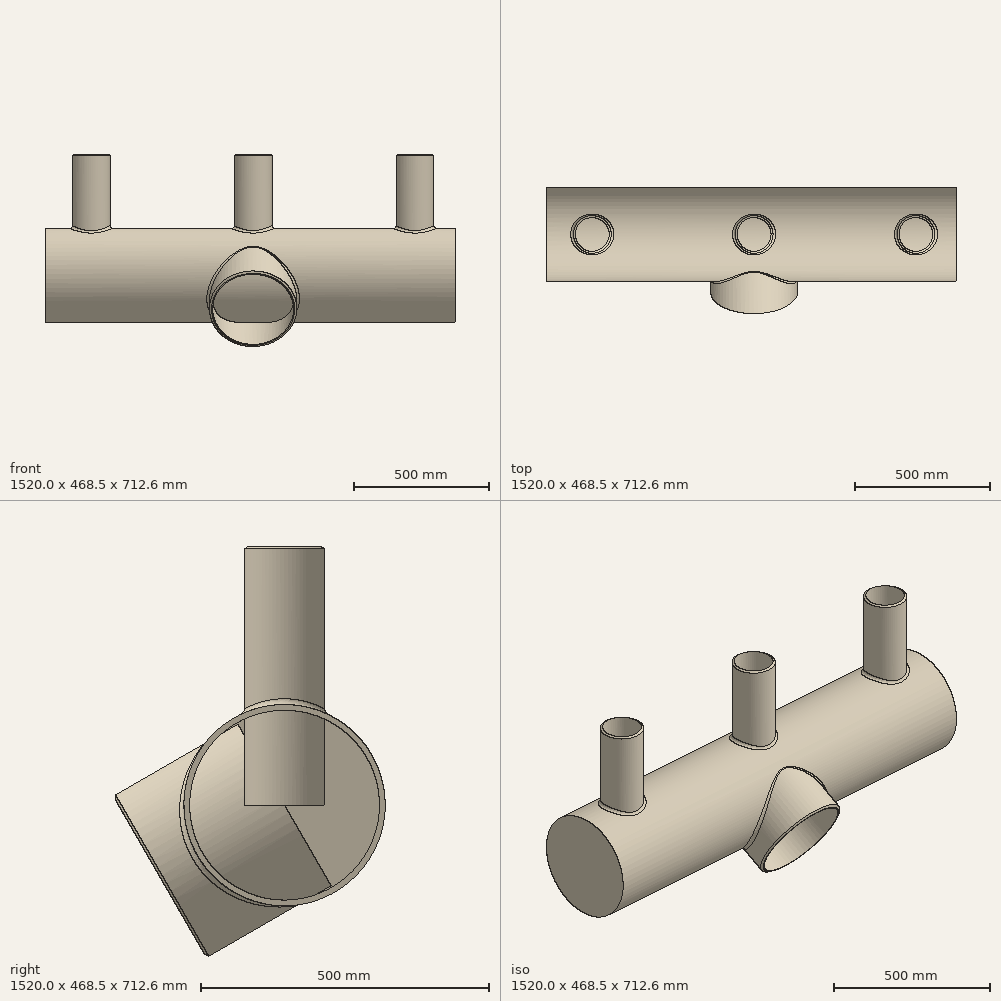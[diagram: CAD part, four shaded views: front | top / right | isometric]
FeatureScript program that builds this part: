
annotation { "Feature Type Name" : "Feature", "Feature Type Description" : "" }
export const myFeature = defineFeature(function(context is Context, id is Id, definition is map)
    precondition{}
    {
        {
            var Q0;
            Q0=qCreatedBy(makeId("Right.planeOp"),FACE);
            var sketch = newSketch(context, id + "F0", { "sketchPlane" : qUnion([Q0])});
            skCircle(sketch, "E0", {"center": v(0, 0) * mm, "radius": 175 * mm});
            skCircle(sketch, "E1", {"center": v(0, 0) * mm, "radius": 165 * mm});
            skSolve(sketch);
        }
        {
            var Q0;
            Q0=makeQuery(id+"F0.imprint","IMPRINT",FACE,{"disambiguationData":[TD([[makeQuery(id+"F0.imprint","IMPRINT",EDGE,{"derivedFrom":sQuery(id+"F0.wireOp",EDGE,"E0")}),1.0]])]});
            extrude(context, id + "F1", {"entities" : qUnion([Q0]), "endBound" : BoundingType.SYMMETRIC, "depth" : 1500 * mm, "offsetDistance" : 25 * mm});
        }
        {
            var Q0;
            Q0=makeQuery(id+"F1.opExtrude","CAP_FACE",FACE,{"disambiguationData":[OSD([sQuery(id+"F0.wireOp",EDGE,"E0"),sQuery(id+"F0.wireOp",EDGE,"E1")])],"isStart":true});
            var sketch = newSketch(context, id + "F2", { "sketchPlane" : qUnion([Q0])});
            skCircle(sketch, "E2.0", {"center": v(0, 0) * mm, "radius": 175 * mm});
            skSolve(sketch);
        }
        {
            var Q0;
            Q0 = qSketchRegion(id + "F2", true);
            extrude(context, id + "F3", {"entities" : qUnion([Q0]), "operationType" : NewBodyOperationType.ADD, "depth" : 20 * mm, "offsetDistance" : 25 * mm});
        }
        {
            var Q0;
            Q0=qCreatedBy(makeId("Top.planeOp"),FACE);
            var sketch = newSketch(context, id + "F4", { "sketchPlane" : qUnion([Q0])});
            skCircle(sketch, "E3", {"center": v(-600, 0) * mm, "radius": 69.85 * mm});
            skCircle(sketch, "E4", {"center": v(0, 0) * mm, "radius": 69.85 * mm});
            skCircle(sketch, "E5", {"center": v(600, 0) * mm, "radius": 69.85 * mm});
            skCircle(sketch, "E6", {"center": v(-600, 0) * mm, "radius": 62.5 * mm});
            skCircle(sketch, "E7", {"center": v(0, 0) * mm, "radius": 62.5 * mm});
            skCircle(sketch, "E8", {"center": v(600, 0) * mm, "radius": 62.5 * mm});
            skSolve(sketch);
        }
        {
            var Q0;
            Q0 = qSketchRegion(id + "F4", true);
            extrude(context, id + "F5", {"entities" : qUnion([Q0]), "operationType" : NewBodyOperationType.ADD, "depth" : 450 * mm, "offsetDistance" : 25 * mm});
        }
        {
            var Q0;
            Q0=qCreatedBy(makeId("Top.planeOp"),FACE);
            var sketch = newSketch(context, id + "F6", { "sketchPlane" : qUnion([Q0])});
            skLineSegment(sketch, "E9", {"start": v(-708.65, 0) * mm, "end": v(764.92, 0) * mm});
            skSolve(sketch);
        }
        {
            var Q0;
            Q0=sQuery(id+"F6.wireOp",EDGE,"E9");
            cPlane(context, id + "F7", {"entities" : qUnion([Q0]), "cplaneType" : CPlaneType.LINE_ANGLE, "offset" : 25 * mm, "angle" : 150 * degree, "oppositeDirection" : true, "width" : 150 * mm, "height" : 150 * mm});
        }
        {
            var Q0;
            Q0=qCreatedBy(id+"F7.planeOp",FACE);
            var sketch = newSketch(context, id + "F8", { "sketchPlane" : qUnion([Q0])});
            skCircle(sketch, "E10", {"center": v(0, 0) * mm, "radius": 161.95 * mm});
            skCircle(sketch, "E11", {"center": v(0, 0) * mm, "radius": 150 * mm});
            skSolve(sketch);
        }
        {
            var Q0;
            Q0 = qSketchRegion(id + "F8", true);
            extrude(context, id + "F9", {"entities" : qUnion([Q0]), "operationType" : NewBodyOperationType.ADD, "depth" : 250 * mm, "offsetDistance" : 25 * mm});
        }
        {
            var Q0;
            {var subQ0=sQuery(id+"F2.wireOp",EDGE,"E2.0");Q0=makeQuery(id+"F9.boolean.opBoolean","INTERSECT",EDGE,{"derivedFrom":[makeQuery(id+"F5.boolean.opBoolean","SPLIT",FACE,{"disambiguationData":[TD([makeQuery(id+"F3.opExtrude","CAP_FACE",FACE,{"disambiguationData":[OSD([subQ0])],"isStart":false})])],"derivedFrom":makeQuery(id+"FQxppkKFvuYUTU2_1.1.F3.boolean.opBoolean","MERGE",FACE,{"derivedFrom":[makeQuery(id+"F3.boolean.opBoolean","MERGE",FACE,{"derivedFrom":[makeQuery(id+"F1.opExtrude","SWEPT_FACE",FACE,{"disambiguationData":[OSD([sQuery(id+"F0.wireOp",EDGE,"E0")])]}),makeQuery(id+"F3.opExtrude","SWEPT_FACE",FACE,{"disambiguationData":[OSD([subQ0])]})]}),makeQuery(id+"FQxppkKFvuYUTU2_1.1.F3.opExtrude","SWEPT_FACE",FACE,{"disambiguationData":[OSD([subQ0])]})]})}),makeQuery(id+"F9.opExtrude","SWEPT_FACE",FACE,{"disambiguationData":[OSD([sQuery(id+"F8.wireOp",EDGE,"E10")])]})]});}
            var Q1;
            {var subQ0=sQuery(id+"F2.wireOp",EDGE,"E2.0");Q1=makeQuery(id+"F5.boolean.opBoolean","INTERSECT",EDGE,{"derivedFrom":[makeQuery(id+"FQxppkKFvuYUTU2_1.1.F3.boolean.opBoolean","MERGE",FACE,{"derivedFrom":[makeQuery(id+"F3.boolean.opBoolean","MERGE",FACE,{"derivedFrom":[makeQuery(id+"F1.opExtrude","SWEPT_FACE",FACE,{"disambiguationData":[OSD([sQuery(id+"F0.wireOp",EDGE,"E0")])]}),makeQuery(id+"F3.opExtrude","SWEPT_FACE",FACE,{"disambiguationData":[OSD([subQ0])]})]}),makeQuery(id+"FQxppkKFvuYUTU2_1.1.F3.opExtrude","SWEPT_FACE",FACE,{"disambiguationData":[OSD([subQ0])]})]}),makeQuery(id+"F5.opExtrude","SWEPT_FACE",FACE,{"disambiguationData":[OSD([sQuery(id+"F4.wireOp",EDGE,"E3")])]})]});}
            var Q2;
            {var subQ0=sQuery(id+"F2.wireOp",EDGE,"E2.0");Q2=makeQuery(id+"F5.boolean.opBoolean","INTERSECT",EDGE,{"derivedFrom":[makeQuery(id+"FQxppkKFvuYUTU2_1.1.F3.boolean.opBoolean","MERGE",FACE,{"derivedFrom":[makeQuery(id+"F3.boolean.opBoolean","MERGE",FACE,{"derivedFrom":[makeQuery(id+"F1.opExtrude","SWEPT_FACE",FACE,{"disambiguationData":[OSD([sQuery(id+"F0.wireOp",EDGE,"E0")])]}),makeQuery(id+"F3.opExtrude","SWEPT_FACE",FACE,{"disambiguationData":[OSD([subQ0])]})]}),makeQuery(id+"FQxppkKFvuYUTU2_1.1.F3.opExtrude","SWEPT_FACE",FACE,{"disambiguationData":[OSD([subQ0])]})]}),makeQuery(id+"F5.opExtrude","SWEPT_FACE",FACE,{"disambiguationData":[OSD([sQuery(id+"F4.wireOp",EDGE,"E4")])]})]});}
            var Q3;
            {var subQ0=sQuery(id+"F2.wireOp",EDGE,"E2.0");Q3=makeQuery(id+"F5.boolean.opBoolean","INTERSECT",EDGE,{"derivedFrom":[makeQuery(id+"FQxppkKFvuYUTU2_1.1.F3.boolean.opBoolean","MERGE",FACE,{"derivedFrom":[makeQuery(id+"F3.boolean.opBoolean","MERGE",FACE,{"derivedFrom":[makeQuery(id+"F1.opExtrude","SWEPT_FACE",FACE,{"disambiguationData":[OSD([sQuery(id+"F0.wireOp",EDGE,"E0")])]}),makeQuery(id+"F3.opExtrude","SWEPT_FACE",FACE,{"disambiguationData":[OSD([subQ0])]})]}),makeQuery(id+"FQxppkKFvuYUTU2_1.1.F3.opExtrude","SWEPT_FACE",FACE,{"disambiguationData":[OSD([subQ0])]})]}),makeQuery(id+"F5.opExtrude","SWEPT_FACE",FACE,{"disambiguationData":[OSD([sQuery(id+"F4.wireOp",EDGE,"E5")])]})]});}
            fillet(context, id + "F10", {"entities" : qUnion([Q0, Q1, Q2, Q3]), "radius" : 10 * mm, "tangentPropagation" : true, "allowEdgeOverflow" : false});
        }
        {
            var Q0;
            Q0=makeQuery(id+"F5.opExtrude","CAP_EDGE",EDGE,{"disambiguationData":[OSD([sQuery(id+"F4.wireOp",EDGE,"E3")])],"isStart":false});
            var Q1;
            Q1=makeQuery(id+"F5.opExtrude","CAP_EDGE",EDGE,{"disambiguationData":[OSD([sQuery(id+"F4.wireOp",EDGE,"E4")])],"isStart":false});
            var Q2;
            Q2=makeQuery(id+"F5.opExtrude","CAP_EDGE",EDGE,{"disambiguationData":[OSD([sQuery(id+"F4.wireOp",EDGE,"E5")])],"isStart":false});
            var Q3;
            Q3=makeQuery(id+"F9.opExtrude","CAP_EDGE",EDGE,{"disambiguationData":[OSD([sQuery(id+"F8.wireOp",EDGE,"E10")])],"isStart":false});
            chamfer(context, id + "F11", {"entities" : qUnion([Q0, Q1, Q2, Q3]), "chamferType" : ChamferType.OFFSET_ANGLE, "width" : 8 * mm, "oppositeDirection" : false, "angle" : 30 * degree, "tangentPropagation" : true});
        }
    });
